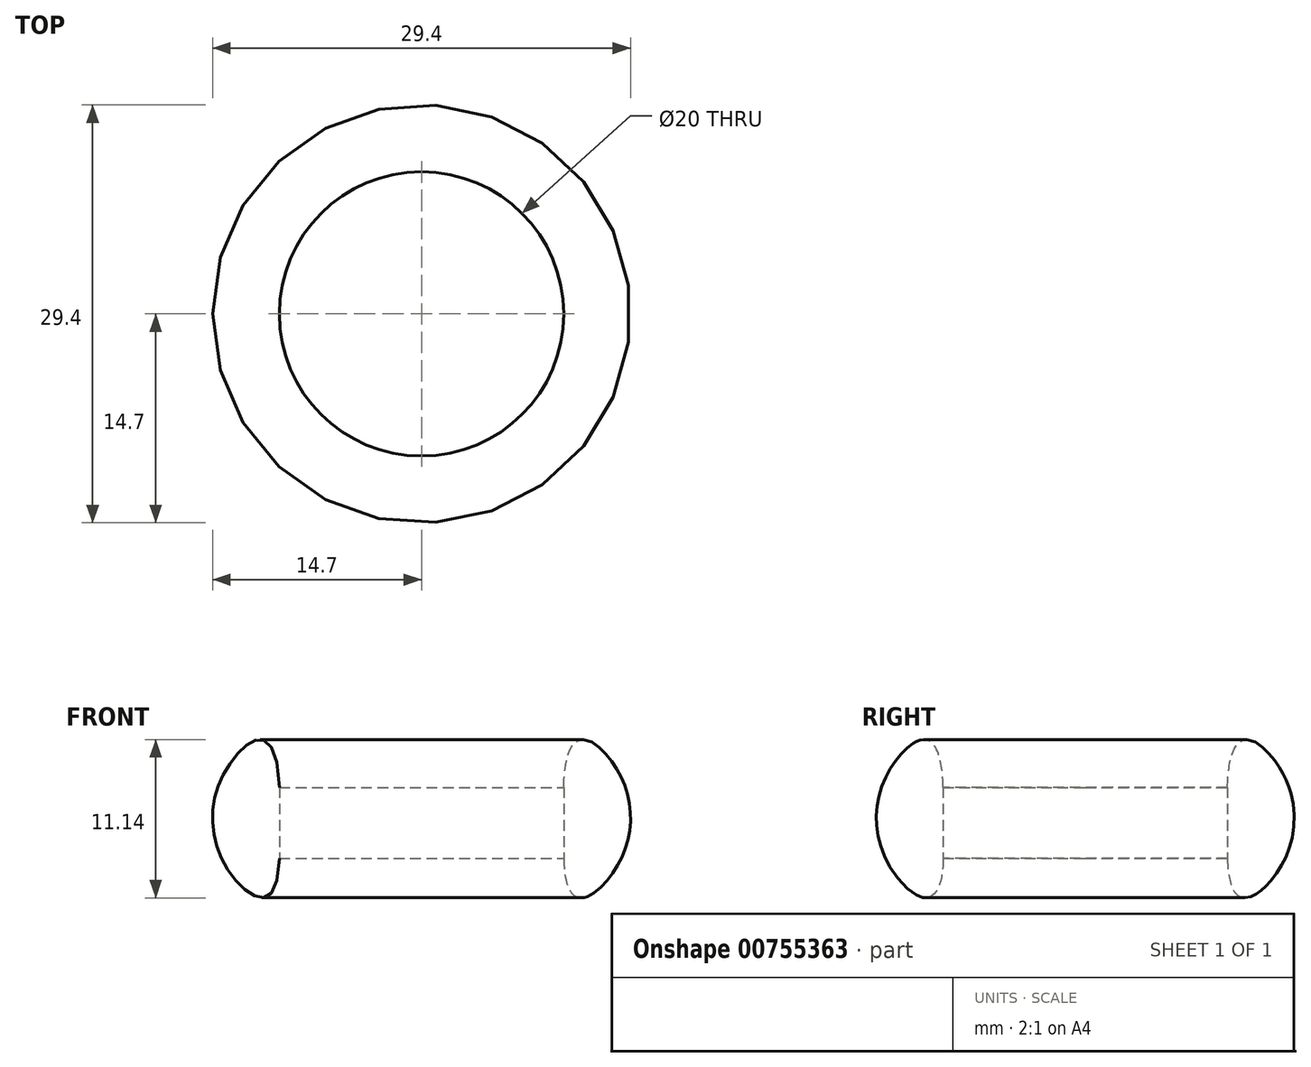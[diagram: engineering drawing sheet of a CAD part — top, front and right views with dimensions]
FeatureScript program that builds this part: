
annotation { "Feature Type Name" : "Feature", "Feature Type Description" : "" }
export const myFeature = defineFeature(function(context is Context, id is Id, definition is map)
    precondition{}
    {
        {
            var Q0;
            Q0=qCreatedBy(makeId("Front.planeOp"),FACE);
            var sketch = newSketch(context, id + "F0", { "sketchPlane" : qUnion([Q0])});
            skLineSegment(sketch, "E0", {"start": v(10, 0) * mm, "end": v(10, -5) * mm});
            skLineSegment(sketch, "E1", {"start": v(0, 0) * mm, "end": v(0, 18.5) * mm});
            skFitSpline(sketch, "E2", {"points": [v(10, 0) * mm, v(13.36, 1.84) * mm, v(13.36, -6.16) * mm, v(10, -5) * mm], "startDerivative": vector(1.43, 49.35) * mm, "endDerivative": vector(-0.95, 44.5) * mm});
            skSolve(sketch);
        }
        {
            var Q0;
            Q0=qSketchRegion(id+"F0",true);
            var Q1;
            Q1=sQuery(id+"F0.wireOp",EDGE,"E1");
            revolve(context, id + "F1", {"surfaceOperationType" : NewSurfaceOperationType.NEW, "entities" : qUnion([Q0]), "axis" : qUnion([Q1]), "revolveType" : RevolveType.FULL});
        }
    });
